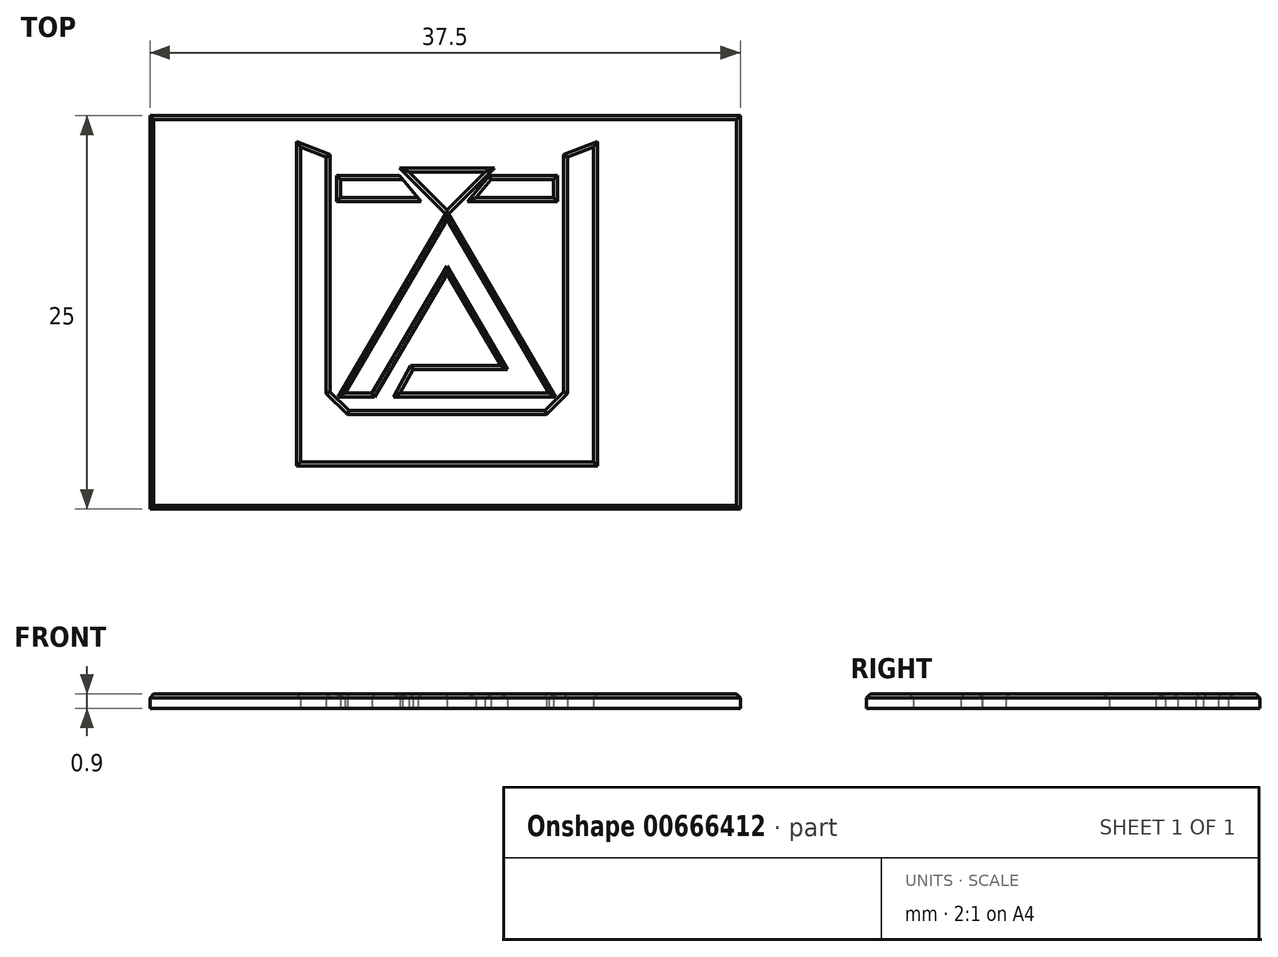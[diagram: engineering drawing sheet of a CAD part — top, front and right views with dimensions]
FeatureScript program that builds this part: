
annotation { "Feature Type Name" : "Feature", "Feature Type Description" : "" }
export const myFeature = defineFeature(function(context is Context, id is Id, definition is map)
    precondition{}
    {
        {
            var Q0;
            Q0=qCreatedBy(makeId("Top.planeOp"),FACE);
            var sketch = newSketch(context, id + "F0", { "sketchPlane" : qUnion([Q0])});
            skLineSegment(sketch, "E0", {"start": v(-9.18, -9.01) * mm, "end": v(-9.18, 10.99) * mm});
            skLineSegment(sketch, "E1", {"start": v(-9.18, 10.99) * mm, "end": v(-7.55, 10.35) * mm});
            skLineSegment(sketch, "E2", {"start": v(-7.55, 10.35) * mm, "end": v(-7.55, -4.65) * mm});
            skLineSegment(sketch, "E3", {"start": v(-7.55, -4.65) * mm, "end": v(-6.2, -6) * mm});
            skLineSegment(sketch, "E4.MirrorCS", {"start": v(9.42, -9.01) * mm, "end": v(9.42, 10.99) * mm});
            skLineSegment(sketch, "E5.MirrorCS", {"start": v(9.42, 10.99) * mm, "end": v(7.79, 10.35) * mm});
            skLineSegment(sketch, "E6.MirrorCS", {"start": v(7.79, 10.35) * mm, "end": v(7.79, -4.65) * mm});
            skLineSegment(sketch, "E7.MirrorCS", {"start": v(7.79, -4.65) * mm, "end": v(6.44, -6) * mm});
            skLineSegment(sketch, "E8", {"start": v(-6.2, -6) * mm, "end": v(6.44, -6) * mm});
            skLineSegment(sketch, "E9", {"start": v(-6.65, 8.94) * mm, "end": v(-2.69, 8.94) * mm});
            skLineSegment(sketch, "E10", {"start": v(-2.69, 8.94) * mm, "end": v(-1.73, 7.8) * mm});
            skLineSegment(sketch, "E11", {"start": v(-6.65, 8.94) * mm, "end": v(-6.65, 7.8) * mm});
            skLineSegment(sketch, "E12", {"start": v(-6.65, 7.8) * mm, "end": v(-1.73, 7.8) * mm});
            skLineSegment(sketch, "E13", {"start": v(-6.36, -4.63) * mm, "end": v(-4.63, -4.63) * mm});
            skLineSegment(sketch, "E14.MirrorCS", {"start": v(2.92, 8.94) * mm, "end": v(1.96, 7.8) * mm});
            skLineSegment(sketch, "E15.MirrorCS", {"start": v(6.89, 7.8) * mm, "end": v(1.96, 7.8) * mm});
            skLineSegment(sketch, "E16.MirrorCS", {"start": v(6.89, 8.94) * mm, "end": v(2.92, 8.94) * mm});
            skLineSegment(sketch, "E17.MirrorCS", {"start": v(6.89, 8.94) * mm, "end": v(6.89, 7.8) * mm});
            skLineSegment(sketch, "E18", {"start": v(6.59, -4.63) * mm, "end": v(-2.86, -4.63) * mm});
            skLineSegment(sketch, "E19", {"start": v(-2.86, -4.63) * mm, "end": v(-2.04, -3.13) * mm});
            skLineSegment(sketch, "E20", {"start": v(3.98, -3.13) * mm, "end": v(0.12, 3.44) * mm});
            skLineSegment(sketch, "E21", {"start": v(-2.04, -3.13) * mm, "end": v(3.98, -3.13) * mm});
            skLineSegment(sketch, "E22", {"start": v(0.12, 3.44) * mm, "end": v(-4.63, -4.63) * mm});
            skLineSegment(sketch, "E23", {"start": v(-6.36, -4.63) * mm, "end": v(0.12, 6.4) * mm});
            skLineSegment(sketch, "E24", {"start": v(0.12, 6.4) * mm, "end": v(6.59, -4.63) * mm});
            skLineSegment(sketch, "E25", {"start": v(-2.3, 9.42) * mm, "end": v(2.53, 9.42) * mm});
            skLineSegment(sketch, "E26", {"start": v(2.53, 9.42) * mm, "end": v(0.12, 7) * mm});
            skLineSegment(sketch, "E27", {"start": v(0.12, 7) * mm, "end": v(-2.3, 9.42) * mm});
            skLineSegment(sketch, "E28", {"start": v(-9.18, -9.01) * mm, "end": v(9.42, -9.01) * mm});
            skSolve(sketch);
        }
        {
            var Q0;
            Q0=qCreatedBy(makeId("Top.planeOp"),FACE);
            var sketch = newSketch(context, id + "F1", { "sketchPlane" : qUnion([Q0])});
            skLineSegment(sketch, "E29", {"start": v(0, -12) * mm, "end": v(18.75, -12) * mm});
            skLineSegment(sketch, "E30", {"start": v(18.75, -12) * mm, "end": v(18.75, 13) * mm});
            skLineSegment(sketch, "E31", {"start": v(18.75, 13) * mm, "end": v(-18.75, 13) * mm});
            skLineSegment(sketch, "E32", {"start": v(-18.75, 13) * mm, "end": v(-18.75, -12) * mm});
            skLineSegment(sketch, "E33", {"start": v(-18.75, -12) * mm, "end": v(0, -12) * mm});
            skSolve(sketch);
        }
        {
            var Q0;
            Q0=makeQuery(id+"F1.imprint","IMPRINT",FACE,{"disambiguationData":[TD([[makeQuery(id+"F1.imprint","IMPRINT",EDGE,{"derivedFrom":sQuery(id+"F1.wireOp",EDGE,"E29")}),1.0]])]});
            extrude(context, id + "F2", {"entities" : qUnion([Q0]), "depth" : 0.9 * mm, "offsetDistance" : 25 * mm});
        }
        {
            var Q0;
            Q0=qSketchRegion(id+"F0",true);
            extrude(context, id + "F3", {"entities" : qUnion([Q0]), "operationType" : NewBodyOperationType.REMOVE, "depth" : 5 * mm, "offsetDistance" : 25 * mm});
        }
        {
            var Q0;
            Q0=makeQuery(id+"F2.opExtrude","CAP_EDGE",EDGE,{"disambiguationData":[OSD([sQuery(id+"F1.wireOp",EDGE,"E32")])],"isStart":false});
            var Q1;
            Q1=makeQuery(id+"F2.opExtrude","CAP_EDGE",EDGE,{"disambiguationData":[OSD([sQuery(id+"F1.wireOp",EDGE,"E31")])],"isStart":false});
            var Q2;
            Q2=makeQuery(id+"F2.opExtrude","CAP_EDGE",EDGE,{"disambiguationData":[OSD([sQuery(id+"F1.wireOp",EDGE,"E30")])],"isStart":false});
            var Q3;
            Q3=makeQuery(id+"F2.opExtrude","CAP_EDGE",EDGE,{"disambiguationData":[OSD([sQuery(id+"F1.wireOp",EDGE,"E29"),sQuery(id+"F1.wireOp",EDGE,"E33")])],"isStart":false});
            var Q4;
            Q4=makeQuery(id+"F3.boolean.opBoolean","INTERSECT",EDGE,{"derivedFrom":[makeQuery(id+"F2.opExtrude","CAP_FACE",FACE,{"disambiguationData":[OSD([sQuery(id+"F1.wireOp",EDGE,"E29"),sQuery(id+"F1.wireOp",EDGE,"E30"),sQuery(id+"F1.wireOp",EDGE,"E31"),sQuery(id+"F1.wireOp",EDGE,"E32"),sQuery(id+"F1.wireOp",EDGE,"E33")])],"isStart":false}),makeQuery(id+"F3.opExtrude","SWEPT_FACE",FACE,{"disambiguationData":[OSD([sQuery(id+"F0.wireOp",EDGE,"E0")])]})]});
            var Q5;
            Q5=makeQuery(id+"F3.boolean.opBoolean","INTERSECT",EDGE,{"derivedFrom":[makeQuery(id+"F2.opExtrude","CAP_FACE",FACE,{"disambiguationData":[OSD([sQuery(id+"F1.wireOp",EDGE,"E29"),sQuery(id+"F1.wireOp",EDGE,"E30"),sQuery(id+"F1.wireOp",EDGE,"E31"),sQuery(id+"F1.wireOp",EDGE,"E32"),sQuery(id+"F1.wireOp",EDGE,"E33")])],"isStart":false}),makeQuery(id+"F3.opExtrude","SWEPT_FACE",FACE,{"disambiguationData":[OSD([sQuery(id+"F0.wireOp",EDGE,"E1")])]})]});
            var Q6;
            Q6=makeQuery(id+"F3.boolean.opBoolean","INTERSECT",EDGE,{"derivedFrom":[makeQuery(id+"F2.opExtrude","CAP_FACE",FACE,{"disambiguationData":[OSD([sQuery(id+"F1.wireOp",EDGE,"E29"),sQuery(id+"F1.wireOp",EDGE,"E30"),sQuery(id+"F1.wireOp",EDGE,"E31"),sQuery(id+"F1.wireOp",EDGE,"E32"),sQuery(id+"F1.wireOp",EDGE,"E33")])],"isStart":false}),makeQuery(id+"F3.opExtrude","SWEPT_FACE",FACE,{"disambiguationData":[OSD([sQuery(id+"F0.wireOp",EDGE,"E2")])]})]});
            var Q7;
            Q7=makeQuery(id+"F3.boolean.opBoolean","INTERSECT",EDGE,{"derivedFrom":[makeQuery(id+"F2.opExtrude","CAP_FACE",FACE,{"disambiguationData":[OSD([sQuery(id+"F1.wireOp",EDGE,"E29"),sQuery(id+"F1.wireOp",EDGE,"E30"),sQuery(id+"F1.wireOp",EDGE,"E31"),sQuery(id+"F1.wireOp",EDGE,"E32"),sQuery(id+"F1.wireOp",EDGE,"E33")])],"isStart":false}),makeQuery(id+"F3.opExtrude","SWEPT_FACE",FACE,{"disambiguationData":[OSD([sQuery(id+"F0.wireOp",EDGE,"E3")])]})]});
            var Q8;
            Q8=makeQuery(id+"F3.boolean.opBoolean","INTERSECT",EDGE,{"derivedFrom":[makeQuery(id+"F2.opExtrude","CAP_FACE",FACE,{"disambiguationData":[OSD([sQuery(id+"F1.wireOp",EDGE,"E29"),sQuery(id+"F1.wireOp",EDGE,"E30"),sQuery(id+"F1.wireOp",EDGE,"E31"),sQuery(id+"F1.wireOp",EDGE,"E32"),sQuery(id+"F1.wireOp",EDGE,"E33")])],"isStart":false}),makeQuery(id+"F3.opExtrude","SWEPT_FACE",FACE,{"disambiguationData":[OSD([sQuery(id+"F0.wireOp",EDGE,"E8")])]})]});
            var Q9;
            Q9=makeQuery(id+"F3.boolean.opBoolean","INTERSECT",EDGE,{"derivedFrom":[makeQuery(id+"F2.opExtrude","CAP_FACE",FACE,{"disambiguationData":[OSD([sQuery(id+"F1.wireOp",EDGE,"E29"),sQuery(id+"F1.wireOp",EDGE,"E30"),sQuery(id+"F1.wireOp",EDGE,"E31"),sQuery(id+"F1.wireOp",EDGE,"E32"),sQuery(id+"F1.wireOp",EDGE,"E33")])],"isStart":false}),makeQuery(id+"F3.opExtrude","SWEPT_FACE",FACE,{"disambiguationData":[OSD([sQuery(id+"F0.wireOp",EDGE,"E7.MirrorCS")])]})]});
            var Q10;
            Q10=makeQuery(id+"F3.boolean.opBoolean","INTERSECT",EDGE,{"derivedFrom":[makeQuery(id+"F2.opExtrude","CAP_FACE",FACE,{"disambiguationData":[OSD([sQuery(id+"F1.wireOp",EDGE,"E29"),sQuery(id+"F1.wireOp",EDGE,"E30"),sQuery(id+"F1.wireOp",EDGE,"E31"),sQuery(id+"F1.wireOp",EDGE,"E32"),sQuery(id+"F1.wireOp",EDGE,"E33")])],"isStart":false}),makeQuery(id+"F3.opExtrude","SWEPT_FACE",FACE,{"disambiguationData":[OSD([sQuery(id+"F0.wireOp",EDGE,"E6.MirrorCS")])]})]});
            var Q11;
            Q11=makeQuery(id+"F3.boolean.opBoolean","INTERSECT",EDGE,{"derivedFrom":[makeQuery(id+"F2.opExtrude","CAP_FACE",FACE,{"disambiguationData":[OSD([sQuery(id+"F1.wireOp",EDGE,"E29"),sQuery(id+"F1.wireOp",EDGE,"E30"),sQuery(id+"F1.wireOp",EDGE,"E31"),sQuery(id+"F1.wireOp",EDGE,"E32"),sQuery(id+"F1.wireOp",EDGE,"E33")])],"isStart":false}),makeQuery(id+"F3.opExtrude","SWEPT_FACE",FACE,{"disambiguationData":[OSD([sQuery(id+"F0.wireOp",EDGE,"E5.MirrorCS")])]})]});
            var Q12;
            Q12=makeQuery(id+"F3.boolean.opBoolean","INTERSECT",EDGE,{"derivedFrom":[makeQuery(id+"F2.opExtrude","CAP_FACE",FACE,{"disambiguationData":[OSD([sQuery(id+"F1.wireOp",EDGE,"E29"),sQuery(id+"F1.wireOp",EDGE,"E30"),sQuery(id+"F1.wireOp",EDGE,"E31"),sQuery(id+"F1.wireOp",EDGE,"E32"),sQuery(id+"F1.wireOp",EDGE,"E33")])],"isStart":false}),makeQuery(id+"F3.opExtrude","SWEPT_FACE",FACE,{"disambiguationData":[OSD([sQuery(id+"F0.wireOp",EDGE,"E4.MirrorCS")])]})]});
            var Q13;
            Q13=makeQuery(id+"F3.boolean.opBoolean","INTERSECT",EDGE,{"derivedFrom":[makeQuery(id+"F2.opExtrude","CAP_FACE",FACE,{"disambiguationData":[OSD([sQuery(id+"F1.wireOp",EDGE,"E29"),sQuery(id+"F1.wireOp",EDGE,"E30"),sQuery(id+"F1.wireOp",EDGE,"E31"),sQuery(id+"F1.wireOp",EDGE,"E32"),sQuery(id+"F1.wireOp",EDGE,"E33")])],"isStart":false}),makeQuery(id+"F3.opExtrude","SWEPT_FACE",FACE,{"disambiguationData":[OSD([sQuery(id+"F0.wireOp",EDGE,"E28")])]})]});
            var Q14;
            Q14=makeQuery(id+"F3.boolean.opBoolean","INTERSECT",EDGE,{"derivedFrom":[makeQuery(id+"F2.opExtrude","CAP_FACE",FACE,{"disambiguationData":[OSD([sQuery(id+"F1.wireOp",EDGE,"E29"),sQuery(id+"F1.wireOp",EDGE,"E30"),sQuery(id+"F1.wireOp",EDGE,"E31"),sQuery(id+"F1.wireOp",EDGE,"E32"),sQuery(id+"F1.wireOp",EDGE,"E33")])],"isStart":false}),makeQuery(id+"F3.opExtrude","SWEPT_FACE",FACE,{"disambiguationData":[OSD([sQuery(id+"F0.wireOp",EDGE,"E23")])]})]});
            var Q15;
            Q15=makeQuery(id+"F3.boolean.opBoolean","INTERSECT",EDGE,{"derivedFrom":[makeQuery(id+"F2.opExtrude","CAP_FACE",FACE,{"disambiguationData":[OSD([sQuery(id+"F1.wireOp",EDGE,"E29"),sQuery(id+"F1.wireOp",EDGE,"E30"),sQuery(id+"F1.wireOp",EDGE,"E31"),sQuery(id+"F1.wireOp",EDGE,"E32"),sQuery(id+"F1.wireOp",EDGE,"E33")])],"isStart":false}),makeQuery(id+"F3.opExtrude","SWEPT_FACE",FACE,{"disambiguationData":[OSD([sQuery(id+"F0.wireOp",EDGE,"E24")])]})]});
            var Q16;
            Q16=makeQuery(id+"F3.boolean.opBoolean","INTERSECT",EDGE,{"derivedFrom":[makeQuery(id+"F2.opExtrude","CAP_FACE",FACE,{"disambiguationData":[OSD([sQuery(id+"F1.wireOp",EDGE,"E29"),sQuery(id+"F1.wireOp",EDGE,"E30"),sQuery(id+"F1.wireOp",EDGE,"E31"),sQuery(id+"F1.wireOp",EDGE,"E32"),sQuery(id+"F1.wireOp",EDGE,"E33")])],"isStart":false}),makeQuery(id+"F3.opExtrude","SWEPT_FACE",FACE,{"disambiguationData":[OSD([sQuery(id+"F0.wireOp",EDGE,"E22")])]})]});
            var Q17;
            Q17=makeQuery(id+"F3.boolean.opBoolean","INTERSECT",EDGE,{"derivedFrom":[makeQuery(id+"F2.opExtrude","CAP_FACE",FACE,{"disambiguationData":[OSD([sQuery(id+"F1.wireOp",EDGE,"E29"),sQuery(id+"F1.wireOp",EDGE,"E30"),sQuery(id+"F1.wireOp",EDGE,"E31"),sQuery(id+"F1.wireOp",EDGE,"E32"),sQuery(id+"F1.wireOp",EDGE,"E33")])],"isStart":false}),makeQuery(id+"F3.opExtrude","SWEPT_FACE",FACE,{"disambiguationData":[OSD([sQuery(id+"F0.wireOp",EDGE,"E20")])]})]});
            var Q18;
            Q18=makeQuery(id+"F3.boolean.opBoolean","INTERSECT",EDGE,{"derivedFrom":[makeQuery(id+"F2.opExtrude","CAP_FACE",FACE,{"disambiguationData":[OSD([sQuery(id+"F1.wireOp",EDGE,"E29"),sQuery(id+"F1.wireOp",EDGE,"E30"),sQuery(id+"F1.wireOp",EDGE,"E31"),sQuery(id+"F1.wireOp",EDGE,"E32"),sQuery(id+"F1.wireOp",EDGE,"E33")])],"isStart":false}),makeQuery(id+"F3.opExtrude","SWEPT_FACE",FACE,{"disambiguationData":[OSD([sQuery(id+"F0.wireOp",EDGE,"E21")])]})]});
            var Q19;
            Q19=makeQuery(id+"F3.boolean.opBoolean","INTERSECT",EDGE,{"derivedFrom":[makeQuery(id+"F2.opExtrude","CAP_FACE",FACE,{"disambiguationData":[OSD([sQuery(id+"F1.wireOp",EDGE,"E29"),sQuery(id+"F1.wireOp",EDGE,"E30"),sQuery(id+"F1.wireOp",EDGE,"E31"),sQuery(id+"F1.wireOp",EDGE,"E32"),sQuery(id+"F1.wireOp",EDGE,"E33")])],"isStart":false}),makeQuery(id+"F3.opExtrude","SWEPT_FACE",FACE,{"disambiguationData":[OSD([sQuery(id+"F0.wireOp",EDGE,"E19")])]})]});
            var Q20;
            Q20=makeQuery(id+"F3.boolean.opBoolean","INTERSECT",EDGE,{"derivedFrom":[makeQuery(id+"F2.opExtrude","CAP_FACE",FACE,{"disambiguationData":[OSD([sQuery(id+"F1.wireOp",EDGE,"E29"),sQuery(id+"F1.wireOp",EDGE,"E30"),sQuery(id+"F1.wireOp",EDGE,"E31"),sQuery(id+"F1.wireOp",EDGE,"E32"),sQuery(id+"F1.wireOp",EDGE,"E33")])],"isStart":false}),makeQuery(id+"F3.opExtrude","SWEPT_FACE",FACE,{"disambiguationData":[OSD([sQuery(id+"F0.wireOp",EDGE,"E18")])]})]});
            var Q21;
            Q21=makeQuery(id+"F3.boolean.opBoolean","INTERSECT",EDGE,{"derivedFrom":[makeQuery(id+"F2.opExtrude","CAP_FACE",FACE,{"disambiguationData":[OSD([sQuery(id+"F1.wireOp",EDGE,"E29"),sQuery(id+"F1.wireOp",EDGE,"E30"),sQuery(id+"F1.wireOp",EDGE,"E31"),sQuery(id+"F1.wireOp",EDGE,"E32"),sQuery(id+"F1.wireOp",EDGE,"E33")])],"isStart":false}),makeQuery(id+"F3.opExtrude","SWEPT_FACE",FACE,{"disambiguationData":[OSD([sQuery(id+"F0.wireOp",EDGE,"E13")])]})]});
            var Q22;
            Q22=makeQuery(id+"F3.boolean.opBoolean","INTERSECT",EDGE,{"derivedFrom":[makeQuery(id+"F2.opExtrude","CAP_FACE",FACE,{"disambiguationData":[OSD([sQuery(id+"F1.wireOp",EDGE,"E29"),sQuery(id+"F1.wireOp",EDGE,"E30"),sQuery(id+"F1.wireOp",EDGE,"E31"),sQuery(id+"F1.wireOp",EDGE,"E32"),sQuery(id+"F1.wireOp",EDGE,"E33")])],"isStart":false}),makeQuery(id+"F3.opExtrude","SWEPT_FACE",FACE,{"disambiguationData":[OSD([sQuery(id+"F0.wireOp",EDGE,"E12")])]})]});
            var Q23;
            Q23=makeQuery(id+"F3.boolean.opBoolean","INTERSECT",EDGE,{"derivedFrom":[makeQuery(id+"F2.opExtrude","CAP_FACE",FACE,{"disambiguationData":[OSD([sQuery(id+"F1.wireOp",EDGE,"E29"),sQuery(id+"F1.wireOp",EDGE,"E30"),sQuery(id+"F1.wireOp",EDGE,"E31"),sQuery(id+"F1.wireOp",EDGE,"E32"),sQuery(id+"F1.wireOp",EDGE,"E33")])],"isStart":false}),makeQuery(id+"F3.opExtrude","SWEPT_FACE",FACE,{"disambiguationData":[OSD([sQuery(id+"F0.wireOp",EDGE,"E11")])]})]});
            var Q24;
            Q24=makeQuery(id+"F3.boolean.opBoolean","INTERSECT",EDGE,{"derivedFrom":[makeQuery(id+"F2.opExtrude","CAP_FACE",FACE,{"disambiguationData":[OSD([sQuery(id+"F1.wireOp",EDGE,"E29"),sQuery(id+"F1.wireOp",EDGE,"E30"),sQuery(id+"F1.wireOp",EDGE,"E31"),sQuery(id+"F1.wireOp",EDGE,"E32"),sQuery(id+"F1.wireOp",EDGE,"E33")])],"isStart":false}),makeQuery(id+"F3.opExtrude","SWEPT_FACE",FACE,{"disambiguationData":[OSD([sQuery(id+"F0.wireOp",EDGE,"E9")])]})]});
            var Q25;
            Q25=makeQuery(id+"F3.boolean.opBoolean","INTERSECT",EDGE,{"derivedFrom":[makeQuery(id+"F2.opExtrude","CAP_FACE",FACE,{"disambiguationData":[OSD([sQuery(id+"F1.wireOp",EDGE,"E29"),sQuery(id+"F1.wireOp",EDGE,"E30"),sQuery(id+"F1.wireOp",EDGE,"E31"),sQuery(id+"F1.wireOp",EDGE,"E32"),sQuery(id+"F1.wireOp",EDGE,"E33")])],"isStart":false}),makeQuery(id+"F3.opExtrude","SWEPT_FACE",FACE,{"disambiguationData":[OSD([sQuery(id+"F0.wireOp",EDGE,"E27")])]})]});
            var Q26;
            Q26=makeQuery(id+"F3.boolean.opBoolean","INTERSECT",EDGE,{"derivedFrom":[makeQuery(id+"F2.opExtrude","CAP_FACE",FACE,{"disambiguationData":[OSD([sQuery(id+"F1.wireOp",EDGE,"E29"),sQuery(id+"F1.wireOp",EDGE,"E30"),sQuery(id+"F1.wireOp",EDGE,"E31"),sQuery(id+"F1.wireOp",EDGE,"E32"),sQuery(id+"F1.wireOp",EDGE,"E33")])],"isStart":false}),makeQuery(id+"F3.opExtrude","SWEPT_FACE",FACE,{"disambiguationData":[OSD([sQuery(id+"F0.wireOp",EDGE,"E25")])]})]});
            var Q27;
            Q27=makeQuery(id+"F3.boolean.opBoolean","INTERSECT",EDGE,{"derivedFrom":[makeQuery(id+"F2.opExtrude","CAP_FACE",FACE,{"disambiguationData":[OSD([sQuery(id+"F1.wireOp",EDGE,"E29"),sQuery(id+"F1.wireOp",EDGE,"E30"),sQuery(id+"F1.wireOp",EDGE,"E31"),sQuery(id+"F1.wireOp",EDGE,"E32"),sQuery(id+"F1.wireOp",EDGE,"E33")])],"isStart":false}),makeQuery(id+"F3.opExtrude","SWEPT_FACE",FACE,{"disambiguationData":[OSD([sQuery(id+"F0.wireOp",EDGE,"E26")])]})]});
            var Q28;
            Q28=makeQuery(id+"F3.boolean.opBoolean","INTERSECT",EDGE,{"derivedFrom":[makeQuery(id+"F2.opExtrude","CAP_FACE",FACE,{"disambiguationData":[OSD([sQuery(id+"F1.wireOp",EDGE,"E29"),sQuery(id+"F1.wireOp",EDGE,"E30"),sQuery(id+"F1.wireOp",EDGE,"E31"),sQuery(id+"F1.wireOp",EDGE,"E32"),sQuery(id+"F1.wireOp",EDGE,"E33")])],"isStart":false}),makeQuery(id+"F3.opExtrude","SWEPT_FACE",FACE,{"disambiguationData":[OSD([sQuery(id+"F0.wireOp",EDGE,"E14.MirrorCS")])]})]});
            var Q29;
            Q29=makeQuery(id+"F3.boolean.opBoolean","INTERSECT",EDGE,{"derivedFrom":[makeQuery(id+"F2.opExtrude","CAP_FACE",FACE,{"disambiguationData":[OSD([sQuery(id+"F1.wireOp",EDGE,"E29"),sQuery(id+"F1.wireOp",EDGE,"E30"),sQuery(id+"F1.wireOp",EDGE,"E31"),sQuery(id+"F1.wireOp",EDGE,"E32"),sQuery(id+"F1.wireOp",EDGE,"E33")])],"isStart":false}),makeQuery(id+"F3.opExtrude","SWEPT_FACE",FACE,{"disambiguationData":[OSD([sQuery(id+"F0.wireOp",EDGE,"E16.MirrorCS")])]})]});
            var Q30;
            Q30=makeQuery(id+"F3.boolean.opBoolean","INTERSECT",EDGE,{"derivedFrom":[makeQuery(id+"F2.opExtrude","CAP_FACE",FACE,{"disambiguationData":[OSD([sQuery(id+"F1.wireOp",EDGE,"E29"),sQuery(id+"F1.wireOp",EDGE,"E30"),sQuery(id+"F1.wireOp",EDGE,"E31"),sQuery(id+"F1.wireOp",EDGE,"E32"),sQuery(id+"F1.wireOp",EDGE,"E33")])],"isStart":false}),makeQuery(id+"F3.opExtrude","SWEPT_FACE",FACE,{"disambiguationData":[OSD([sQuery(id+"F0.wireOp",EDGE,"E15.MirrorCS")])]})]});
            var Q31;
            Q31=makeQuery(id+"F3.boolean.opBoolean","INTERSECT",EDGE,{"derivedFrom":[makeQuery(id+"F2.opExtrude","CAP_FACE",FACE,{"disambiguationData":[OSD([sQuery(id+"F1.wireOp",EDGE,"E29"),sQuery(id+"F1.wireOp",EDGE,"E30"),sQuery(id+"F1.wireOp",EDGE,"E31"),sQuery(id+"F1.wireOp",EDGE,"E32"),sQuery(id+"F1.wireOp",EDGE,"E33")])],"isStart":false}),makeQuery(id+"F3.opExtrude","SWEPT_FACE",FACE,{"disambiguationData":[OSD([sQuery(id+"F0.wireOp",EDGE,"E17.MirrorCS")])]})]});
            chamfer(context, id + "F4", {"entities" : qUnion([Q0, Q1, Q2, Q3, Q4, Q5, Q6, Q7, Q8, Q9, Q10, Q11, Q12, Q13, Q14, Q15, Q16, Q17, Q18, Q19, Q20, Q21, Q22, Q23, Q24, Q25, Q26, Q27, Q28, Q29, Q30, Q31]), "width" : 0.25 * mm, "tangentPropagation" : true});
        }
    });
